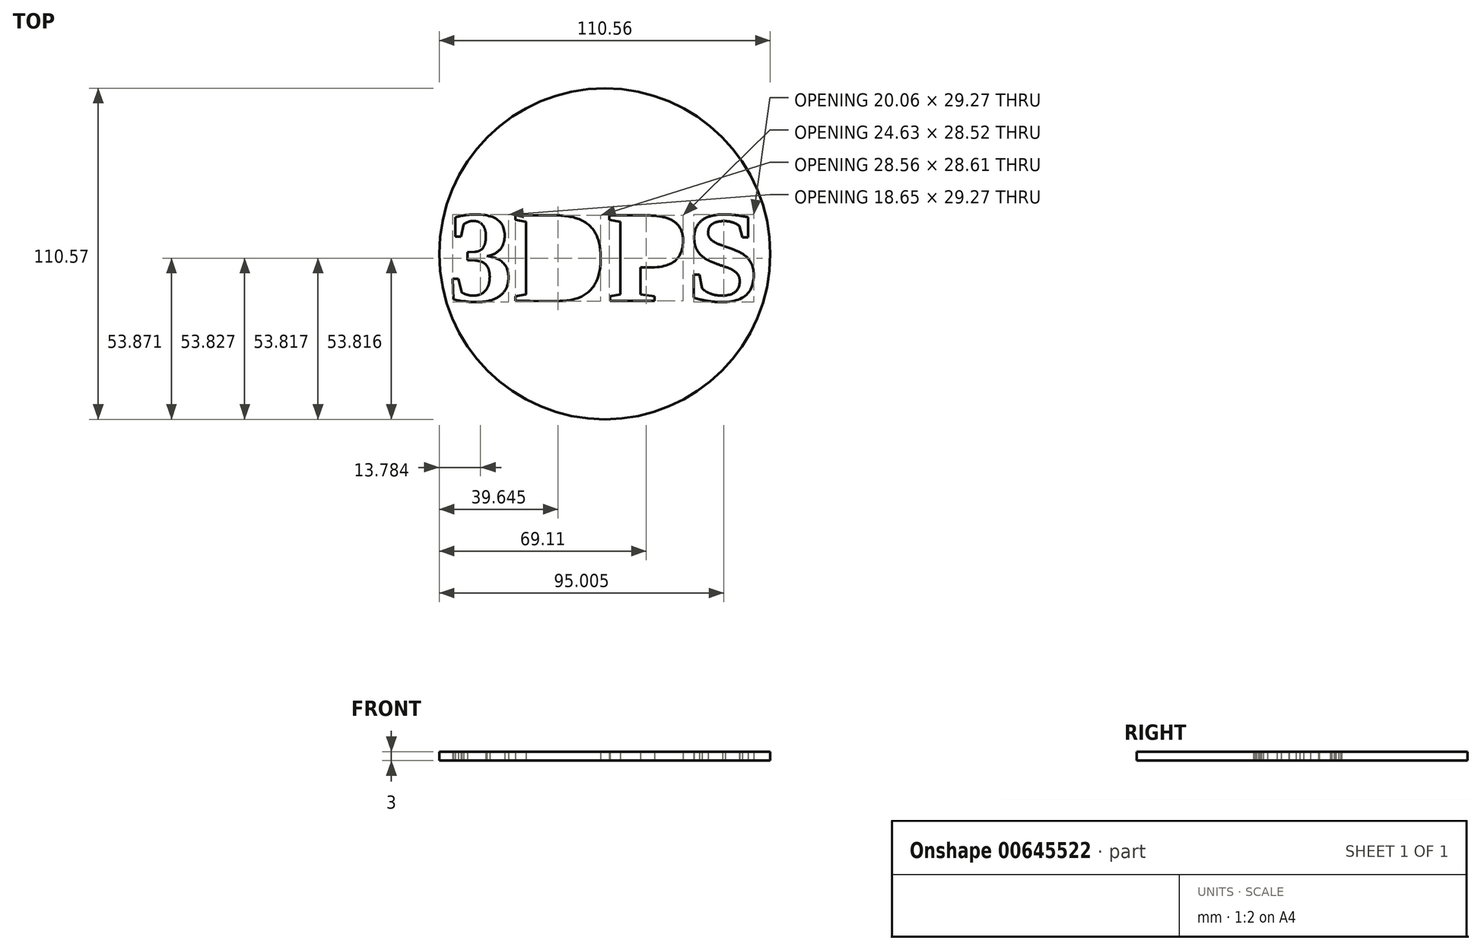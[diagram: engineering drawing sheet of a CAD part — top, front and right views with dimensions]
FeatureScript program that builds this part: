
annotation { "Feature Type Name" : "Feature", "Feature Type Description" : "" }
export const myFeature = defineFeature(function(context is Context, id is Id, definition is map)
    precondition{}
    {
        {
            var Q0;
            Q0=qCreatedBy(makeId("Top.planeOp"),FACE);
            var sketch = newSketch(context, id + "F0", { "sketchPlane" : qUnion([Q0])});
            skText(sketch, "E0", { "text": "3DPS\n", "fontName": "Tinos-Bold.ttf"});
            skCircle(sketch, "E1", {"center": v(8.3, 24.41) * mm, "radius": 55.28 * mm});
            const initialGuessF0  = {"E0": [-0.04416, 0.00874, 1, 0, 0.03136]};
            skSetInitialGuess(sketch, initialGuessF0);
            skSolve(sketch);
        }
        {
            var Q0;
            Q0=makeQuery(id+"F0.imprint","IMPRINT",FACE,{"disambiguationData":[TD([[makeQuery(id+"F0.imprint","IMPRINT",EDGE,{"derivedFrom":sQuery(id+"F0.wireOp",EDGE,"E0.sketch_text.stroke-0")}),1.0]])]});
            extrude(context, id + "F1", {"entities" : qUnion([Q0]), "depth" : 3 * mm, "offsetDistance" : 25 * mm});
        }
    });
